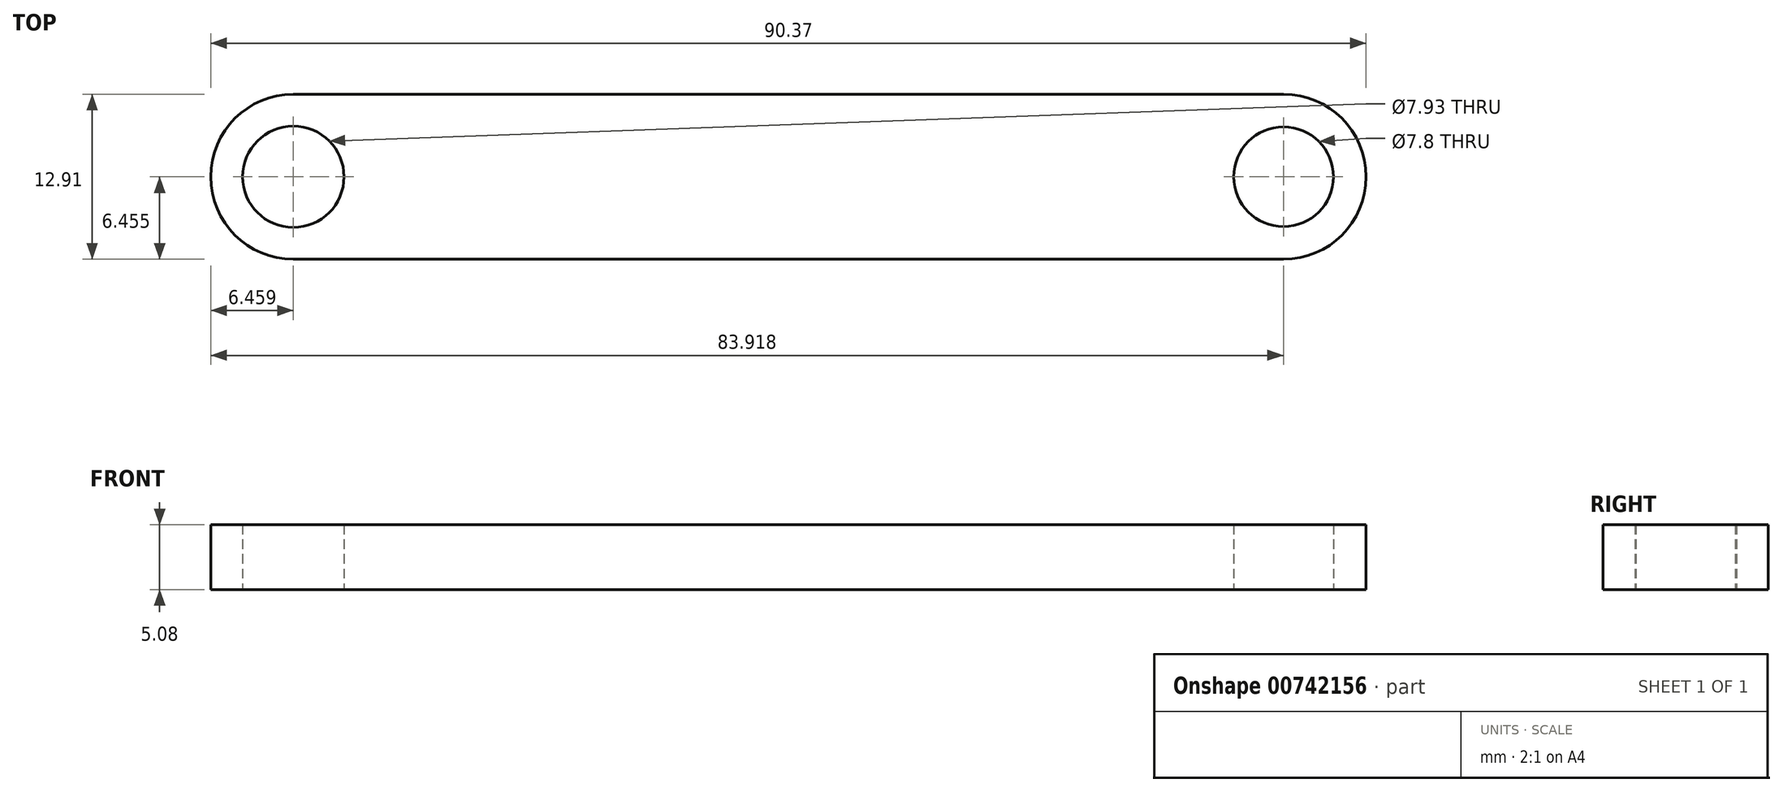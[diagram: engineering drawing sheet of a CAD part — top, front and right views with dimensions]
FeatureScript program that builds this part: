
annotation { "Feature Type Name" : "Feature", "Feature Type Description" : "" }
export const myFeature = defineFeature(function(context is Context, id is Id, definition is map)
    precondition{}
    {
        {
            var Q0;
            Q0=qCreatedBy(makeId("Top.planeOp"),FACE);
            var sketch = newSketch(context, id + "F0", { "sketchPlane" : qUnion([Q0])});
            skLineSegment(sketch, "E0.bottom", {"start": v(-83.93, -6.9) * mm, "end": v(-6.47, -6.9) * mm});
            skLineSegment(sketch, "E0.top", {"start": v(-83.93, -19.82) * mm, "end": v(-6.47, -19.82) * mm});
            skLineSegment(sketch, "E0.left", {"start": v(-90.39, -13.36) * mm, "end": v(-90.39, -13.36) * mm});
            skLineSegment(sketch, "E0.right", {"start": v(-0.02, -13.36) * mm, "end": v(-0.02, -13.36) * mm});
            skPoint(sketch, "E1.visualSharp", {"position": v(-90.39, -6.9) * mm});
            skArc(sketch, "E1.filletArc", {"start": v(-83.93, -6.9) * mm, "mid": v(-88.5, -8.8) * mm, "end": v(-90.39, -13.36) * mm});
            skPoint(sketch, "E2.visualSharp", {"position": v(-90.39, -19.82) * mm});
            skArc(sketch, "E2.filletArc", {"start": v(-90.39, -13.36) * mm, "mid": v(-88.5, -17.93) * mm, "end": v(-83.93, -19.82) * mm});
            skPoint(sketch, "E3.visualSharp", {"position": v(-0.02, -6.9) * mm});
            skArc(sketch, "E3.filletArc", {"start": v(-0.02, -13.36) * mm, "mid": v(-1.9, -8.8) * mm, "end": v(-6.47, -6.9) * mm});
            skPoint(sketch, "E4.visualSharp", {"position": v(-0.02, -19.82) * mm});
            skArc(sketch, "E4.filletArc", {"start": v(-6.47, -19.82) * mm, "mid": v(-1.9, -17.93) * mm, "end": v(-0.02, -13.36) * mm});
            skCircle(sketch, "E5", {"center": v(-83.93, -13.36) * mm, "radius": 3.97 * mm});
            skCircle(sketch, "E6", {"center": v(-6.47, -13.36) * mm, "radius": 3.9 * mm});
            skSolve(sketch);
        }
        {
            var Q0;
            Q0=makeQuery(id+"F0.imprint","IMPRINT",FACE,{"disambiguationData":[TD([[makeQuery(id+"F0.imprint","IMPRINT",EDGE,{"derivedFrom":sQuery(id+"F0.wireOp",EDGE,"E0.bottom")}),-1.0]])]});
            extrude(context, id + "F1", {"entities" : qUnion([Q0]), "depth" : 5.08 * mm, "offsetDistance" : 25.4 * mm});
        }
    });
